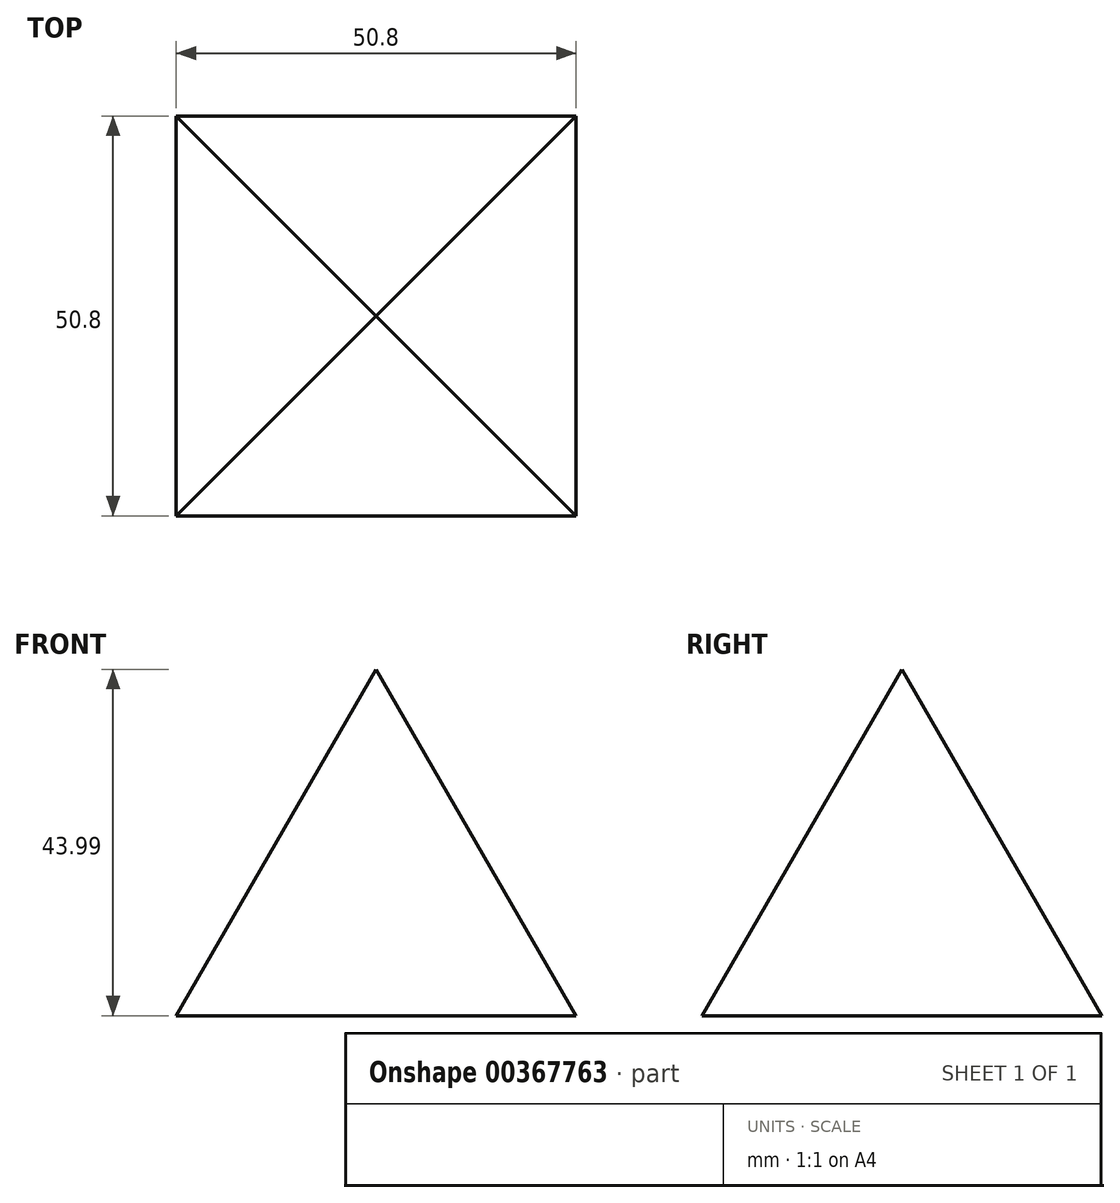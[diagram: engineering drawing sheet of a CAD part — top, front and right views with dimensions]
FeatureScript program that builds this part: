
annotation { "Feature Type Name" : "Feature", "Feature Type Description" : "" }
export const myFeature = defineFeature(function(context is Context, id is Id, definition is map)
    precondition{}
    {
        {
            var Q0;
            Q0=qCreatedBy(makeId("Top.planeOp"),FACE);
            var sketch = newSketch(context, id + "F0", { "sketchPlane" : qUnion([Q0])});
            skLineSegment(sketch, "E0.bottom", {"start": v(25.4, 25.4) * mm, "end": v(-25.4, 25.4) * mm});
            skLineSegment(sketch, "E0.top", {"start": v(25.4, -25.4) * mm, "end": v(-25.4, -25.4) * mm});
            skLineSegment(sketch, "E0.left", {"start": v(25.4, 25.4) * mm, "end": v(25.4, -25.4) * mm});
            skLineSegment(sketch, "E0.right", {"start": v(-25.4, 25.4) * mm, "end": v(-25.4, -25.4) * mm});
            skPoint(sketch, "E0.middle", {"position": v(0, 0) * mm});
            skSolve(sketch);
        }
        {
            var Q0;
            Q0=makeQuery(id+"F0.imprint","IMPRINT",FACE,{"disambiguationData":[TD([[makeQuery(id+"F0.imprint","IMPRINT",EDGE,{"derivedFrom":sQuery(id+"F0.wireOp",EDGE,"E0.bottom")}),1.0]])]});
            extrude(context, id + "F1", {"entities" : qUnion([Q0]), "depth" : 50.8 * mm, "hasDraft" : true, "draftAngle" : 30 * degree, "draftPullDirection" : true});
        }
    });
